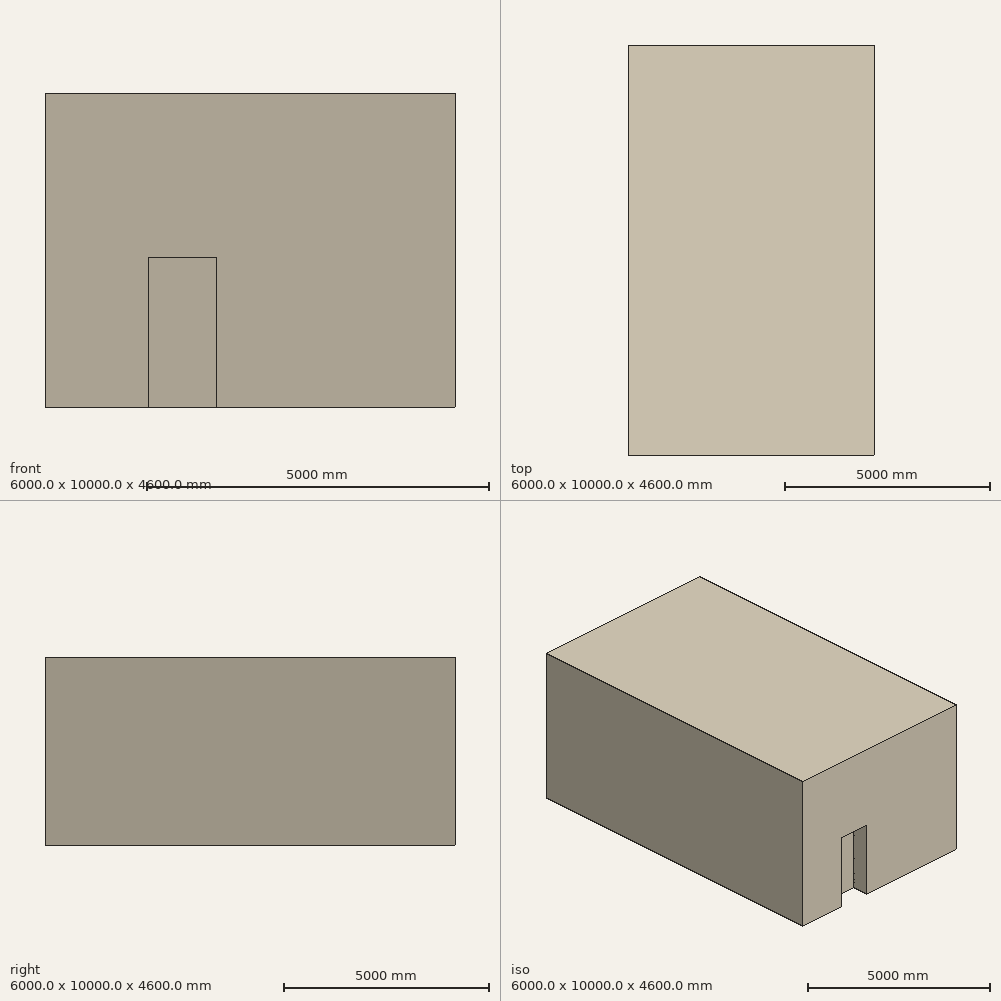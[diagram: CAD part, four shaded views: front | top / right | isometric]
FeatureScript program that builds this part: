
annotation { "Feature Type Name" : "Feature", "Feature Type Description" : "" }
export const myFeature = defineFeature(function(context is Context, id is Id, definition is map)
    precondition{}
    {
        {
            var Q0;
            Q0=qCreatedBy(makeId("Top.planeOp"),FACE);
            var sketch = newSketch(context, id + "F0", { "sketchPlane" : qUnion([Q0])});
            skLineSegment(sketch, "E0.bottom", {"start": v(0, 0) * mm, "end": v(6000, 0) * mm});
            skLineSegment(sketch, "E0.top", {"start": v(0, 10000) * mm, "end": v(6000, 10000) * mm});
            skLineSegment(sketch, "E0.left", {"start": v(0, 0) * mm, "end": v(0, 10000) * mm});
            skLineSegment(sketch, "E0.right", {"start": v(6000, 0) * mm, "end": v(6000, 10000) * mm});
            skSolve(sketch);
        }
        {
            var Q0;
            Q0=makeQuery(id+"F0.imprint","IMPRINT",FACE,{"disambiguationData":[TD([[makeQuery(id+"F0.imprint","IMPRINT",EDGE,{"derivedFrom":sQuery(id+"F0.wireOp",EDGE,"E0.bottom")}),1.0]])]});
            extrude(context, id + "F1", {"entities" : qUnion([Q0]), "depth" : 25 * mm, "offsetDistance" : 25 * mm});
        }
        {
            var Q0;
            Q0=makeQuery(id+"F0.imprint","IMPRINT",FACE,{"disambiguationData":[TD([[makeQuery(id+"F0.imprint","IMPRINT",EDGE,{"derivedFrom":sQuery(id+"F0.wireOp",EDGE,"E0.bottom")}),1.0]])]});
            extrude(context, id + "F2", {"entities" : qUnion([Q0]), "operationType" : NewBodyOperationType.ADD, "depth" : 5000 * mm, "offsetDistance" : 25 * mm});
        }
        {
            var Q0;
            Q0=makeQuery(id+"F2.opExtrude","CAP_FACE",FACE,{"disambiguationData":[OSD([sQuery(id+"F0.wireOp",EDGE,"E0.bottom"),sQuery(id+"F0.wireOp",EDGE,"E0.top"),sQuery(id+"F0.wireOp",EDGE,"E0.left"),sQuery(id+"F0.wireOp",EDGE,"E0.right")])],"isStart":false});
            cPlane(context, id + "F3", {"entities" : qUnion([Q0]), "cplaneType" : CPlaneType.OFFSET, "offset" : 400 * mm, "oppositeDirection" : true, "width" : 150 * mm, "height" : 150 * mm});
        }
        {
            var Q0;
            Q0=qCreatedBy(id+"F3.planeOp",FACE);
            var sketch = newSketch(context, id + "F4", { "sketchPlane" : qUnion([Q0])});
            skLineSegment(sketch, "E1.0", {"start": v(0, 0) * mm, "end": v(0, 10000) * mm});
            skLineSegment(sketch, "E2.0", {"start": v(6000, 0) * mm, "end": v(6000, 10000) * mm});
            skLineSegment(sketch, "E3.0", {"start": v(0, 0) * mm, "end": v(6000, 0) * mm});
            skLineSegment(sketch, "E4.0", {"start": v(0, 10000) * mm, "end": v(6000, 10000) * mm});
            skSolve(sketch);
        }
        {
            var Q0;
            Q0 = qSketchRegion(id + "F4", true);
            extrude(context, id + "F5", {"entities" : qUnion([Q0]), "operationType" : NewBodyOperationType.REMOVE, "endBound" : BoundingType.THROUGH_ALL, "depth" : 25 * mm, "offsetDistance" : 25 * mm});
        }
        {
            var Q0;
            {var subQ0=sQuery(id+"F0.wireOp",EDGE,"E0.bottom");Q0=makeQuery(id+"F2.boolean.opBoolean","MERGE",FACE,{"derivedFrom":[makeQuery(id+"F1.opExtrude","SWEPT_FACE",FACE,{"disambiguationData":[OSD([subQ0])]}),makeQuery(id+"F2.opExtrude","SWEPT_FACE",FACE,{"disambiguationData":[OSD([subQ0])]})]});}
            var sketch = newSketch(context, id + "F6", { "sketchPlane" : qUnion([Q0])});
            skLineSegment(sketch, "E5.0", {"start": v(0, 0) * mm, "end": v(6000, 0) * mm});
            skLineSegment(sketch, "E6.0", {"start": v(6000, 4600) * mm, "end": v(6000, 0) * mm});
            skSolve(sketch);
        }
        {
            var Q0;
            Q0=makeQuery(id+"F6.imprint","IMPRINT",FACE,{"disambiguationData":[TD([[makeQuery(id+"F6.imprint","IMPRINT",EDGE,{"derivedFrom":sQuery(id+"F6.wireOp",EDGE,"E5.0")}),1.0]])]});
            var sketch = newSketch(context, id + "F7", { "sketchPlane" : qUnion([Q0])});
            skLineSegment(sketch, "E7.bottom", {"start": v(1500, 0) * mm, "end": v(2500, 0) * mm});
            skLineSegment(sketch, "E7.top", {"start": v(1500, 2200) * mm, "end": v(2500, 2200) * mm});
            skLineSegment(sketch, "E7.left", {"start": v(1500, 0) * mm, "end": v(1500, 2200) * mm});
            skLineSegment(sketch, "E7.right", {"start": v(2500, 0) * mm, "end": v(2500, 2200) * mm});
            skSolve(sketch);
        }
        {
            var Q0;
            Q0 = qSketchRegion(id + "F7", true);
            var Q1;
            Q1=makeQuery(id+"F9O7JYcMoFSrIbj_1.opShell","OFFSET_FACE",FACE,{"disambiguationData":[OSD([sQuery(id+"F0.wireOp",EDGE,"E0.bottom")])]});
            extrude(context, id + "F8", {"entities" : qUnion([Q0, Q1]), "operationType" : NewBodyOperationType.REMOVE, "oppositeDirection" : true, "depth" : 500 * mm, "offsetDistance" : 25 * mm});
        }
    });
